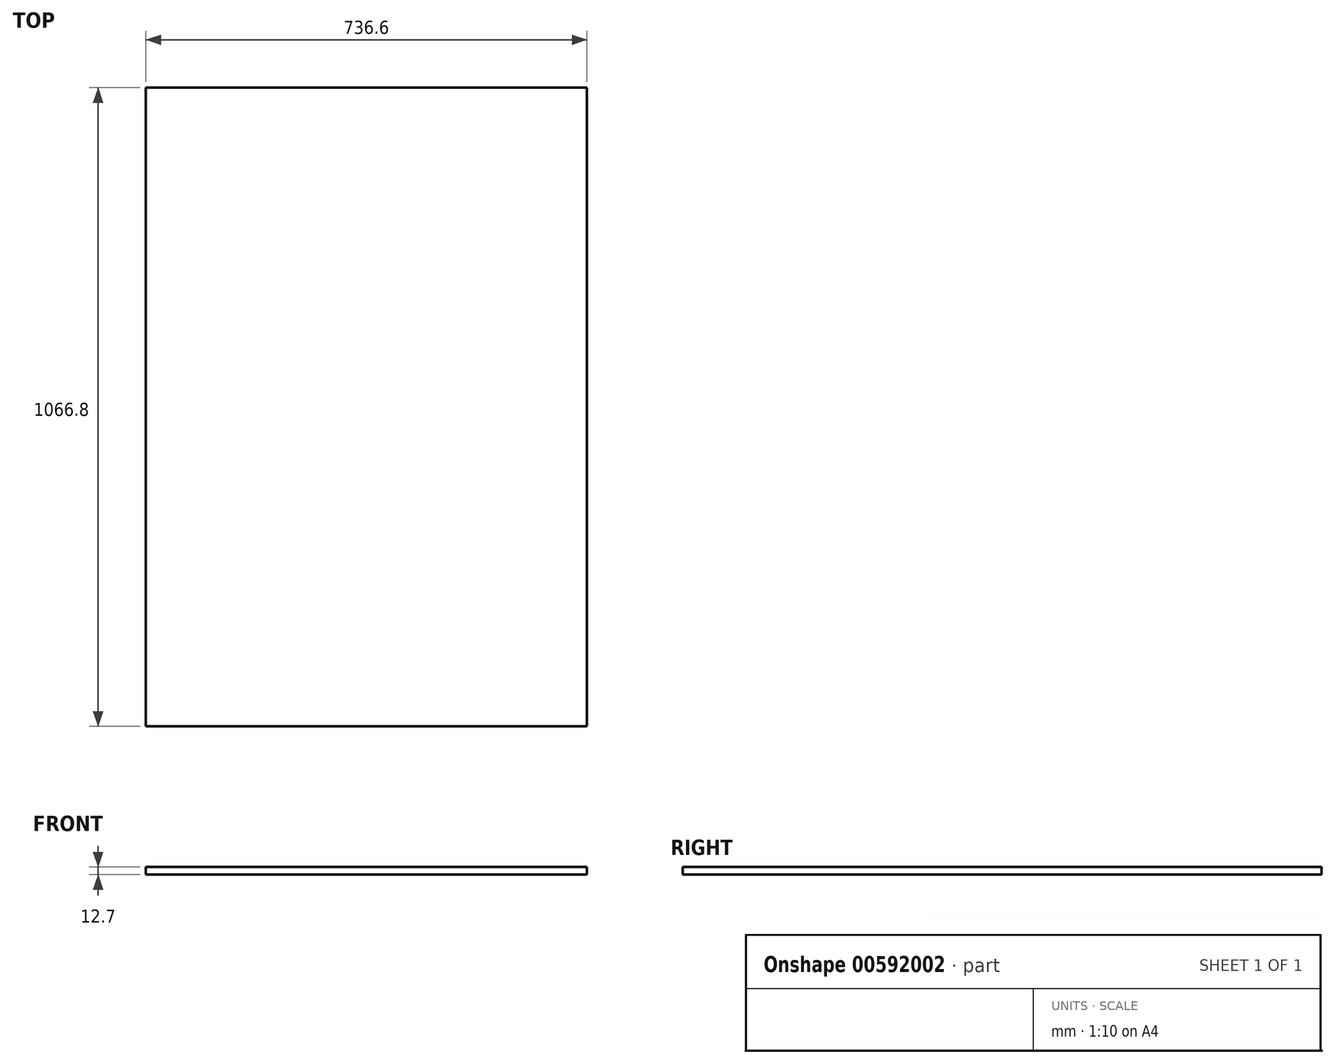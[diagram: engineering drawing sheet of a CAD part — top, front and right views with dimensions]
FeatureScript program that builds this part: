
annotation { "Feature Type Name" : "Feature", "Feature Type Description" : "" }
export const myFeature = defineFeature(function(context is Context, id is Id, definition is map)
    precondition{}
    {
        {
            var Q0;
            Q0=qCreatedBy(makeId("Top.planeOp"),FACE);
            var sketch = newSketch(context, id + "F0", { "sketchPlane" : qUnion([Q0])});
            skLineSegment(sketch, "E0.bottom", {"start": v(-74.17, 1038.38) * mm, "end": v(662.43, 1038.38) * mm});
            skLineSegment(sketch, "E0.top", {"start": v(-74.17, -28.42) * mm, "end": v(662.43, -28.42) * mm});
            skLineSegment(sketch, "E0.left", {"start": v(-74.17, 1038.38) * mm, "end": v(-74.17, -28.42) * mm});
            skLineSegment(sketch, "E0.right", {"start": v(662.43, 1038.38) * mm, "end": v(662.43, -28.42) * mm});
            skSolve(sketch);
        }
        {
            var Q0;
            Q0 = qSketchRegion(id + "F0", true);
            extrude(context, id + "F1", {"entities" : qUnion([Q0]), "endBound" : BoundingType.SYMMETRIC, "depth" : 12.7 * mm, "offsetDistance" : 25.4 * mm});
        }
    });
